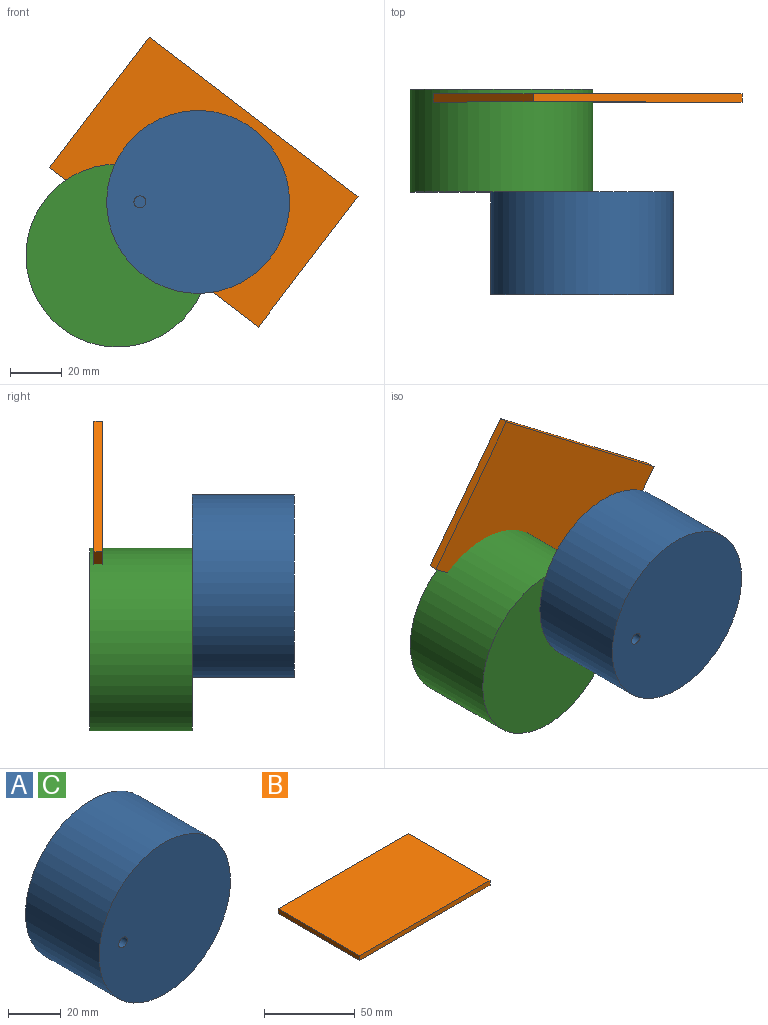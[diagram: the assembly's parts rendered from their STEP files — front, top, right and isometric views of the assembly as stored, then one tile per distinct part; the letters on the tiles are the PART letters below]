
ASSEMBLY  parts=3 mates=3
PART A: 5 faces, bbox 70.7x39.6x70.7 mm
  f0: cylinder r=35.35mm len=70.71mm, axis (0,1,0), area 8801.9mm2, adj f1,f2
  f1: plane 70.71x70.71mm, normal (0,-1,0), area 3909.9mm2, adj f0,f3
  f2: plane 70.71x70.71mm, normal (0,1,0), area 3926.7mm2, adj f0
  f3: cylinder r=2.32mm len=25.4mm, axis (0,-1,0), area 369.6mm2, adj f1,f4
  f4: plane 4.63x4.63mm, normal (0,-1,0), area 16.9mm2, adj f3
PART B: 6 faces, bbox 101.6x63.5x3.2 mm
  f0: plane 101.6x3.18mm, normal (0,1,0), area 322.6mm2, adj f1,f3,f4,f5
  f1: plane 63.5x3.18mm, normal (-1,0,0), area 201.6mm2, adj f0,f2,f4,f5
  f2: plane 101.6x3.18mm, normal (0,-1,0), area 322.6mm2, adj f1,f3,f4,f5
  f3: plane 63.5x3.18mm, normal (1,0,0), area 201.6mm2, adj f0,f2,f4,f5
  f4: plane 101.6x63.5mm, normal (0,0,1), area 6451.6mm2, adj f0,f1,f2,f3
  f5: plane 101.6x63.5mm, normal (0,0,-1), area 6451.6mm2, adj f0,f1,f2,f3
PART C: same geometry as A
PLACE A t=(-95.5,11.11,-40.54)mm fixed
PLACE B rot(axis=(0.9,0.3,-0.3),95.9deg) t=(-92.1,49.01,7.8)mm
PLACE C rot(axis=(0.55,0,-0.83),180deg) t=(-123.69,11.11,-59.27)mm
MATE planar C.f0 <-> A.f0  axis (0,-1,0) through (-124.54,11.11,-61.27)mm
MATE cylindrical C.f3 <-> A.f3  axis (0,-1,0) through (-115.82,25.33,-40.54)mm
MATE parallel B.f4 <-> C.f1  axis (0,-1,0) through (-91.16,45.83,-32.85)mm
